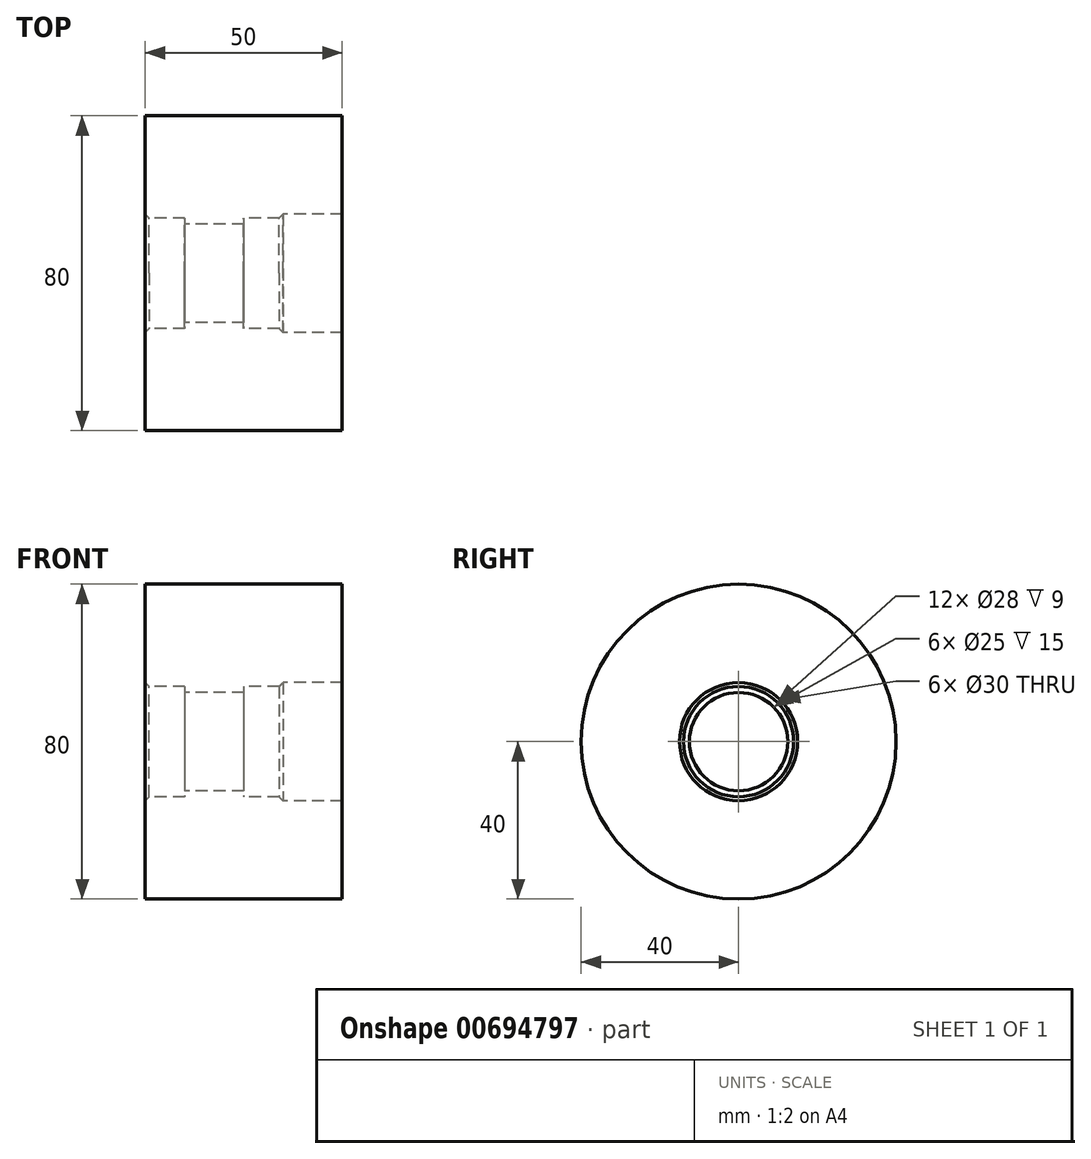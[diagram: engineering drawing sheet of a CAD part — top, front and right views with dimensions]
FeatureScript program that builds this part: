
annotation { "Feature Type Name" : "Feature", "Feature Type Description" : "" }
export const myFeature = defineFeature(function(context is Context, id is Id, definition is map)
    precondition{}
    {
        {
            var Q0;
            Q0=qCreatedBy(makeId("Front.planeOp"),FACE);
            var sketch = newSketch(context, id + "F0", { "sketchPlane" : qUnion([Q0])});
            skLineSegment(sketch, "E0", {"start": v(-50, 40) * mm, "end": v(-50, 14) * mm});
            skLineSegment(sketch, "E1", {"start": v(-50, 14) * mm, "end": v(-40, 14) * mm});
            skLineSegment(sketch, "E2", {"start": v(-40, 14) * mm, "end": v(-40, 12.5) * mm});
            skLineSegment(sketch, "E3", {"start": v(-40, 12.5) * mm, "end": v(-25, 12.5) * mm});
            skLineSegment(sketch, "E4", {"start": v(-25, 12.5) * mm, "end": v(-25, 14) * mm});
            skLineSegment(sketch, "E5", {"start": v(-25, 14) * mm, "end": v(-15, 14) * mm});
            skLineSegment(sketch, "E6", {"start": v(0, 15) * mm, "end": v(0, 40) * mm});
            skLineSegment(sketch, "E7", {"start": v(0, 40) * mm, "end": v(-50, 40) * mm});
            skLineSegment(sketch, "E8", {"start": v(-47.1, 0) * mm, "end": v(11.92, 0) * mm});
            skLineSegment(sketch, "E9", {"start": v(0, 15) * mm, "end": v(-15, 15) * mm});
            skLineSegment(sketch, "E10", {"start": v(-15, 15) * mm, "end": v(-15, 14) * mm});
            skLineSegment(sketch, "E11", {"start": v(-45, 40) * mm, "end": v(-45, 25) * mm});
            skLineSegment(sketch, "E12", {"start": v(-45, 25) * mm, "end": v(-5, 25) * mm});
            skLineSegment(sketch, "E13", {"start": v(-5, 25) * mm, "end": v(-5, 40) * mm});
            skSolve(sketch);
        }
        {
            var Q0;
            Q0=makeQuery(id+"F0.imprint","IMPRINT",FACE,{"disambiguationData":[TD([[makeQuery(id+"F0.imprint","IMPRINT",EDGE,{"derivedFrom":sQuery(id+"F0.wireOp",EDGE,"E0")}),1.0]])]});
            var Q1;
            {var subQ0=sQuery(id+"F0.wireOp",EDGE,"E11");Q1=makeQuery(id+"F0.imprint","IMPRINT",FACE,{"disambiguationData":[TD([[makeQuery(id+"F0.imprint","IMPRINT",EDGE,{"derivedFrom":subQ0}),1.0]])]});}
            var Q2;
            Q2=sQuery(id+"F0.wireOp",EDGE,"E8");
            revolve(context, id + "F1", {"entities" : qUnion([Q0, Q1]), "axis" : qUnion([Q2]), "revolveType" : RevolveType.FULL});
        }
        {
            var Q0;
            Q0=makeQuery(id+"F1.opRevolve","SWEPT_EDGE",EDGE,{"disambiguationData":[OSD([sQuery(id+"F0.wireOp",EDGE,"E5"),sQuery(id+"F0.wireOp",EDGE,"E10")])]});
            var Q1;
            Q1=makeQuery(id+"F1.opRevolve","SWEPT_EDGE",EDGE,{"disambiguationData":[OSD([sQuery(id+"F0.wireOp",EDGE,"E0"),sQuery(id+"F0.wireOp",EDGE,"E1")])]});
            chamfer(context, id + "F2", {"entities" : qUnion([Q0, Q1]), "width" : 1 * mm, "tangentPropagation" : true});
        }
    });
